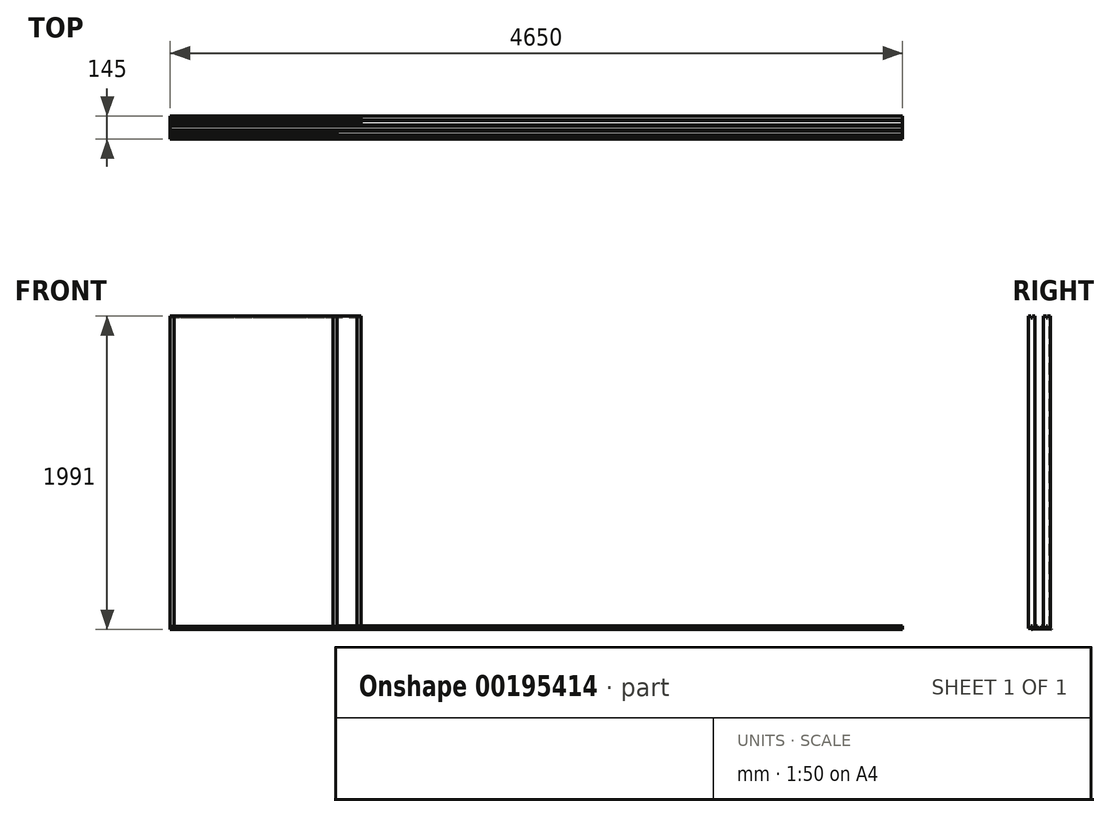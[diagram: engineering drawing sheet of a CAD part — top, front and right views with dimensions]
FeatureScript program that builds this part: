
annotation { "Feature Type Name" : "Feature", "Feature Type Description" : "" }
export const myFeature = defineFeature(function(context is Context, id is Id, definition is map)
    precondition{}
    {
        {
            var Q0;
            Q0=qCreatedBy(makeId("Right.planeOp"),FACE);
            var sketch = newSketch(context, id + "F0", { "sketchPlane" : qUnion([Q0])});
            skLineSegment(sketch, "E0", {"start": v(-100, 0) * mm, "end": v(-221, 4.23) * mm});
            skLineSegment(sketch, "E1", {"start": v(-221, 21) * mm, "end": v(-221, 7.23) * mm});
            skLineSegment(sketch, "E2", {"start": v(-221, 7.23) * mm, "end": v(-194, 6.28) * mm});
            skLineSegment(sketch, "E3", {"start": v(-194, 6.28) * mm, "end": v(-194, 21) * mm});
            skLineSegment(sketch, "E4", {"start": v(-194, 21) * mm, "end": v(-189, 21) * mm});
            skLineSegment(sketch, "E5", {"start": v(-189, 21) * mm, "end": v(-189, 6.1) * mm});
            skLineSegment(sketch, "E6", {"start": v(-189, 6.1) * mm, "end": v(-162, 5.17) * mm});
            skLineSegment(sketch, "E7", {"start": v(-162, 5.17) * mm, "end": v(-162, 21) * mm});
            skLineSegment(sketch, "E8", {"start": v(-162, 21) * mm, "end": v(-157, 21) * mm});
            skLineSegment(sketch, "E9", {"start": v(-157, 21) * mm, "end": v(-157, 5) * mm});
            skLineSegment(sketch, "E10", {"start": v(-157, 5) * mm, "end": v(-130, 4.05) * mm});
            skLineSegment(sketch, "E11", {"start": v(-130, 4.05) * mm, "end": v(-130, 21) * mm});
            skLineSegment(sketch, "E12", {"start": v(-130, 21) * mm, "end": v(-125, 21) * mm});
            skLineSegment(sketch, "E13", {"start": v(-125, 21) * mm, "end": v(-125, 3.87) * mm});
            skLineSegment(sketch, "E14", {"start": v(-125, 3.87) * mm, "end": v(-100, 3) * mm});
            skLineSegment(sketch, "E15", {"start": v(-100, 3) * mm, "end": v(-100, 0) * mm});
            skLineSegment(sketch, "E16", {"start": v(-221, 21) * mm, "end": v(-226, 21) * mm});
            skLineSegment(sketch, "E17", {"start": v(-226, 21) * mm, "end": v(-226, 7.4) * mm});
            skLineSegment(sketch, "E18", {"start": v(-226, 7.4) * mm, "end": v(-240, 7.9) * mm});
            skLineSegment(sketch, "E19", {"start": v(-240, 7.9) * mm, "end": v(-240, 18) * mm});
            skLineSegment(sketch, "E20", {"start": v(-240, 18) * mm, "end": v(-245, 18) * mm});
            skLineSegment(sketch, "E21", {"start": v(-245, 18) * mm, "end": v(-245, 5.06) * mm});
            skLineSegment(sketch, "E22", {"start": v(-226, 4.4) * mm, "end": v(-226, 0) * mm});
            skLineSegment(sketch, "E23", {"start": v(-226, 0) * mm, "end": v(-221, 0) * mm});
            skLineSegment(sketch, "E24", {"start": v(-221, 0) * mm, "end": v(-221, 4.23) * mm});
            skLineSegment(sketch, "E25.trimOffspring", {"start": v(-226, 4.4) * mm, "end": v(-245, 5.06) * mm});
            skLineSegment(sketch, "E26", {"start": v(-127.5, 23) * mm, "end": v(-123, 23) * mm});
            skLineSegment(sketch, "E27", {"start": v(-123, 23) * mm, "end": v(-123, 9) * mm});
            skLineSegment(sketch, "E28", {"start": v(-123, 9) * mm, "end": v(-106.5, 9) * mm});
            skLineSegment(sketch, "E29", {"start": v(-106.5, 9) * mm, "end": v(-106.5, 1000) * mm});
            skLineSegment(sketch, "E30", {"start": v(-127.5, 23) * mm, "end": v(-127.5, 21) * mm, "construction": true});
            skLineSegment(sketch, "E31", {"start": v(-106.5, 1000) * mm, "end": v(-121.16, 1000) * mm, "construction": true});
            skLineSegment(sketch, "E32.MirrorCS", {"start": v(-148.5, 9) * mm, "end": v(-148.5, 1000) * mm});
            skLineSegment(sketch, "E33.MirrorCS", {"start": v(-132, 9) * mm, "end": v(-148.5, 9) * mm});
            skLineSegment(sketch, "E34.MirrorCS", {"start": v(-127.5, 23) * mm, "end": v(-132, 23) * mm});
            skLineSegment(sketch, "E35.MirrorCS", {"start": v(-132, 23) * mm, "end": v(-132, 9) * mm});
            skLineSegment(sketch, "E36.MirrorCS", {"start": v(-148.5, 1991) * mm, "end": v(-148.5, 1000) * mm});
            skLineSegment(sketch, "E37.MirrorCS", {"start": v(-132, 1991) * mm, "end": v(-148.5, 1991) * mm});
            skLineSegment(sketch, "E38.MirrorCS", {"start": v(-132, 1977) * mm, "end": v(-132, 1991) * mm});
            skLineSegment(sketch, "E39.MirrorCS", {"start": v(-123, 1977) * mm, "end": v(-123, 1991) * mm});
            skLineSegment(sketch, "E40.MirrorCS", {"start": v(-127.5, 1977) * mm, "end": v(-132, 1977) * mm});
            skLineSegment(sketch, "E41.MirrorCS", {"start": v(-127.5, 1977) * mm, "end": v(-123, 1977) * mm});
            skLineSegment(sketch, "E42.MirrorCS", {"start": v(-106.5, 1991) * mm, "end": v(-106.5, 1000) * mm});
            skLineSegment(sketch, "E43.MirrorCS", {"start": v(-123, 1991) * mm, "end": v(-106.5, 1991) * mm});
            skLineSegment(sketch, "E44", {"start": v(-112.5, 9) * mm, "end": v(-112.5, 1991) * mm});
            skLineSegment(sketch, "E45.MirrorCS", {"start": v(-142.5, 9) * mm, "end": v(-142.5, 1991) * mm});
            skLineSegment(sketch, "E46", {"start": v(-175.5, 5.64) * mm, "end": v(-175.5, 23.42) * mm, "construction": true});
            skLineSegment(sketch, "E47.MirrorCS", {"start": v(-219, 1991) * mm, "end": v(-202.5, 1991) * mm});
            skLineSegment(sketch, "E48.MirrorCS", {"start": v(-219, 1977) * mm, "end": v(-219, 1991) * mm});
            skLineSegment(sketch, "E49.MirrorCS", {"start": v(-223.5, 1977) * mm, "end": v(-219, 1977) * mm});
            skLineSegment(sketch, "E50.MirrorCS", {"start": v(-223.5, 1977) * mm, "end": v(-228, 1977) * mm});
            skLineSegment(sketch, "E51.MirrorCS", {"start": v(-228, 1977) * mm, "end": v(-228, 1991) * mm});
            skLineSegment(sketch, "E52.MirrorCS", {"start": v(-228, 1991) * mm, "end": v(-244.5, 1991) * mm});
            skLineSegment(sketch, "E53.MirrorCS", {"start": v(-244.5, 1991) * mm, "end": v(-244.5, 1000) * mm});
            skLineSegment(sketch, "E54.MirrorCS", {"start": v(-202.5, 1991) * mm, "end": v(-202.5, 1000) * mm});
            skLineSegment(sketch, "E55.MirrorCS", {"start": v(-223.5, 23) * mm, "end": v(-219, 23) * mm});
            skLineSegment(sketch, "E56.MirrorCS", {"start": v(-223.5, 23) * mm, "end": v(-228, 23) * mm});
            skLineSegment(sketch, "E57.MirrorCS", {"start": v(-244.5, 9) * mm, "end": v(-244.5, 1000) * mm});
            skLineSegment(sketch, "E58.MirrorCS", {"start": v(-228, 23) * mm, "end": v(-228, 9) * mm});
            skLineSegment(sketch, "E59.MirrorCS", {"start": v(-219, 9) * mm, "end": v(-202.5, 9) * mm});
            skLineSegment(sketch, "E60.MirrorCS", {"start": v(-238.5, 9) * mm, "end": v(-238.5, 1991) * mm});
            skLineSegment(sketch, "E61.MirrorCS", {"start": v(-208.5, 9) * mm, "end": v(-208.5, 1991) * mm});
            skLineSegment(sketch, "E62.MirrorCS", {"start": v(-219, 23) * mm, "end": v(-219, 9) * mm});
            skLineSegment(sketch, "E63.MirrorCS", {"start": v(-228, 9) * mm, "end": v(-244.5, 9) * mm});
            skLineSegment(sketch, "E64.MirrorCS", {"start": v(-202.5, 9) * mm, "end": v(-202.5, 1000) * mm});
            skSolve(sketch);
        }
        {
            var Q0;
            Q0=makeQuery(id+"F0.imprint","IMPRINT",FACE,{"disambiguationData":[TD([[makeQuery(id+"F0.imprint","IMPRINT",EDGE,{"derivedFrom":sQuery(id+"F0.wireOp",EDGE,"E0")}),-1.0]])]});
            var Q1;
            {var subQ0=sQuery(id+"F0.wireOp",EDGE,"E63.MirrorCS");var subQ1=sQuery(id+"F0.wireOp",EDGE,"E19");var subQ2=makeQuery(id+"F0.imprint","INTERSECT",VERTEX,{"derivedFrom":[subQ1,subQ0]});Q1=makeQuery(id+"F0.imprint","IMPRINT",FACE,{"disambiguationData":[TD([[makeQuery(id+"F0.imprint","IMPRINT",EDGE,{"disambiguationData":[TD([[subQ2,-1.0]])],"derivedFrom":subQ1}),1.0]])]});}
            extrude(context, id + "F1", {"entities" : qUnion([Q0, Q1]), "depth" : 4650 * mm, "offsetDistance" : 25 * mm});
        }
        {
            var Q0;
            Q0=makeQuery(id+"F0.imprint","IMPRINT",FACE,{"disambiguationData":[TD([[makeQuery(id+"F0.imprint","IMPRINT",EDGE,{"derivedFrom":sQuery(id+"F0.wireOp",EDGE,"E26")}),1.0]])]});
            extrude(context, id + "F2", {"entities" : qUnion([Q0]), "depth" : 1210 * mm, "offsetDistance" : 25 * mm});
        }
        {
            var Q0;
            {var subQ3=sQuery(id+"F0.wireOp",EDGE,"E29");Q0=makeQuery(id+"F0.imprint","IMPRINT",FACE,{"disambiguationData":[TD([[makeQuery(id+"F0.imprint","IMPRINT",EDGE,{"derivedFrom":subQ3}),1.0]])]});}
            var Q1;
            {var subQ4=sQuery(id+"F0.wireOp",EDGE,"E32.MirrorCS");Q1=makeQuery(id+"F0.imprint","IMPRINT",FACE,{"disambiguationData":[TD([[makeQuery(id+"F0.imprint","IMPRINT",EDGE,{"derivedFrom":subQ4}),-1.0]])]});}
            extrude(context, id + "F3", {"entities" : qUnion([Q0, Q1]), "operationType" : NewBodyOperationType.ADD, "depth" : 25 * mm, "offsetDistance" : 25 * mm});
        }
        {
            var Q0;
            {var subQ3=sQuery(id+"F0.wireOp",EDGE,"E29");Q0=makeQuery(id+"F0.imprint","IMPRINT",FACE,{"disambiguationData":[TD([[makeQuery(id+"F0.imprint","IMPRINT",EDGE,{"derivedFrom":subQ3}),1.0]])]});}
            var Q1;
            {var subQ4=sQuery(id+"F0.wireOp",EDGE,"E32.MirrorCS");Q1=makeQuery(id+"F0.imprint","IMPRINT",FACE,{"disambiguationData":[TD([[makeQuery(id+"F0.imprint","IMPRINT",EDGE,{"derivedFrom":subQ4}),-1.0]])]});}
            var Q2;
            Q2=makeQuery(id+"F2.opExtrude","CAP_FACE",FACE,{"disambiguationData":[OSD([sQuery(id+"F0.wireOp",EDGE,"E26"),sQuery(id+"F0.wireOp",EDGE,"E27"),sQuery(id+"F0.wireOp",EDGE,"E28"),sQuery(id+"F0.wireOp",EDGE,"E33.MirrorCS"),sQuery(id+"F0.wireOp",EDGE,"E34.MirrorCS"),sQuery(id+"F0.wireOp",EDGE,"E35.MirrorCS"),sQuery(id+"F0.wireOp",EDGE,"E37.MirrorCS"),sQuery(id+"F0.wireOp",EDGE,"E38.MirrorCS"),sQuery(id+"F0.wireOp",EDGE,"E39.MirrorCS"),sQuery(id+"F0.wireOp",EDGE,"E40.MirrorCS"),sQuery(id+"F0.wireOp",EDGE,"E41.MirrorCS"),sQuery(id+"F0.wireOp",EDGE,"E43.MirrorCS"),sQuery(id+"F0.wireOp",EDGE,"E44"),sQuery(id+"F0.wireOp",EDGE,"E45.MirrorCS")])],"isStart":false});
            extrude(context, id + "F4", {"entities" : qUnion([Q0, Q1]), "operationType" : NewBodyOperationType.ADD, "depth" : 1210 * mm, "endBoundEntityFace" : qUnion([Q2]), "hasOffset" : true, "offsetDistance" : 25 * mm, "hasSecondDirection" : true, "secondDirectionOppositeDirection" : false, "secondDirectionDepth" : (1210 - 25) * mm});
        }
        {
            var Q0;
            {var subQ3=sQuery(id+"F0.wireOp",EDGE,"E48.MirrorCS");Q0=makeQuery(id+"F0.imprint","IMPRINT",FACE,{"disambiguationData":[TD([[makeQuery(id+"F0.imprint","IMPRINT",EDGE,{"derivedFrom":subQ3}),-1.0]])]});}
            extrude(context, id + "F5", {"entities" : qUnion([Q0]), "depth" : 1060 * mm, "offsetDistance" : 25 * mm});
        }
        {
            var Q0;
            {var subQ1=sQuery(id+"F0.wireOp",EDGE,"E54.MirrorCS");Q0=makeQuery(id+"F0.imprint","IMPRINT",FACE,{"disambiguationData":[TD([[makeQuery(id+"F0.imprint","IMPRINT",EDGE,{"derivedFrom":subQ1}),-1.0]])]});}
            var Q1;
            {var subQ0=sQuery(id+"F0.wireOp",EDGE,"E53.MirrorCS");Q1=makeQuery(id+"F0.imprint","IMPRINT",FACE,{"disambiguationData":[TD([[makeQuery(id+"F0.imprint","IMPRINT",EDGE,{"derivedFrom":subQ0}),1.0]])]});}
            extrude(context, id + "F6", {"entities" : qUnion([Q0, Q1]), "operationType" : NewBodyOperationType.ADD, "depth" : 25 * mm, "offsetDistance" : 25 * mm});
        }
        {
            var Q0;
            {var subQ1=sQuery(id+"F0.wireOp",EDGE,"E54.MirrorCS");Q0=makeQuery(id+"F0.imprint","IMPRINT",FACE,{"disambiguationData":[TD([[makeQuery(id+"F0.imprint","IMPRINT",EDGE,{"derivedFrom":subQ1}),-1.0]])]});}
            var Q1;
            {var subQ0=sQuery(id+"F0.wireOp",EDGE,"E53.MirrorCS");Q1=makeQuery(id+"F0.imprint","IMPRINT",FACE,{"disambiguationData":[TD([[makeQuery(id+"F0.imprint","IMPRINT",EDGE,{"derivedFrom":subQ0}),1.0]])]});}
            extrude(context, id + "F7", {"entities" : qUnion([Q0, Q1]), "operationType" : NewBodyOperationType.ADD, "depth" : 1060 * mm, "offsetDistance" : 25 * mm, "hasSecondDirection" : true, "secondDirectionOppositeDirection" : false, "secondDirectionDepth" : (1060 - 25) * mm});
        }
    });
